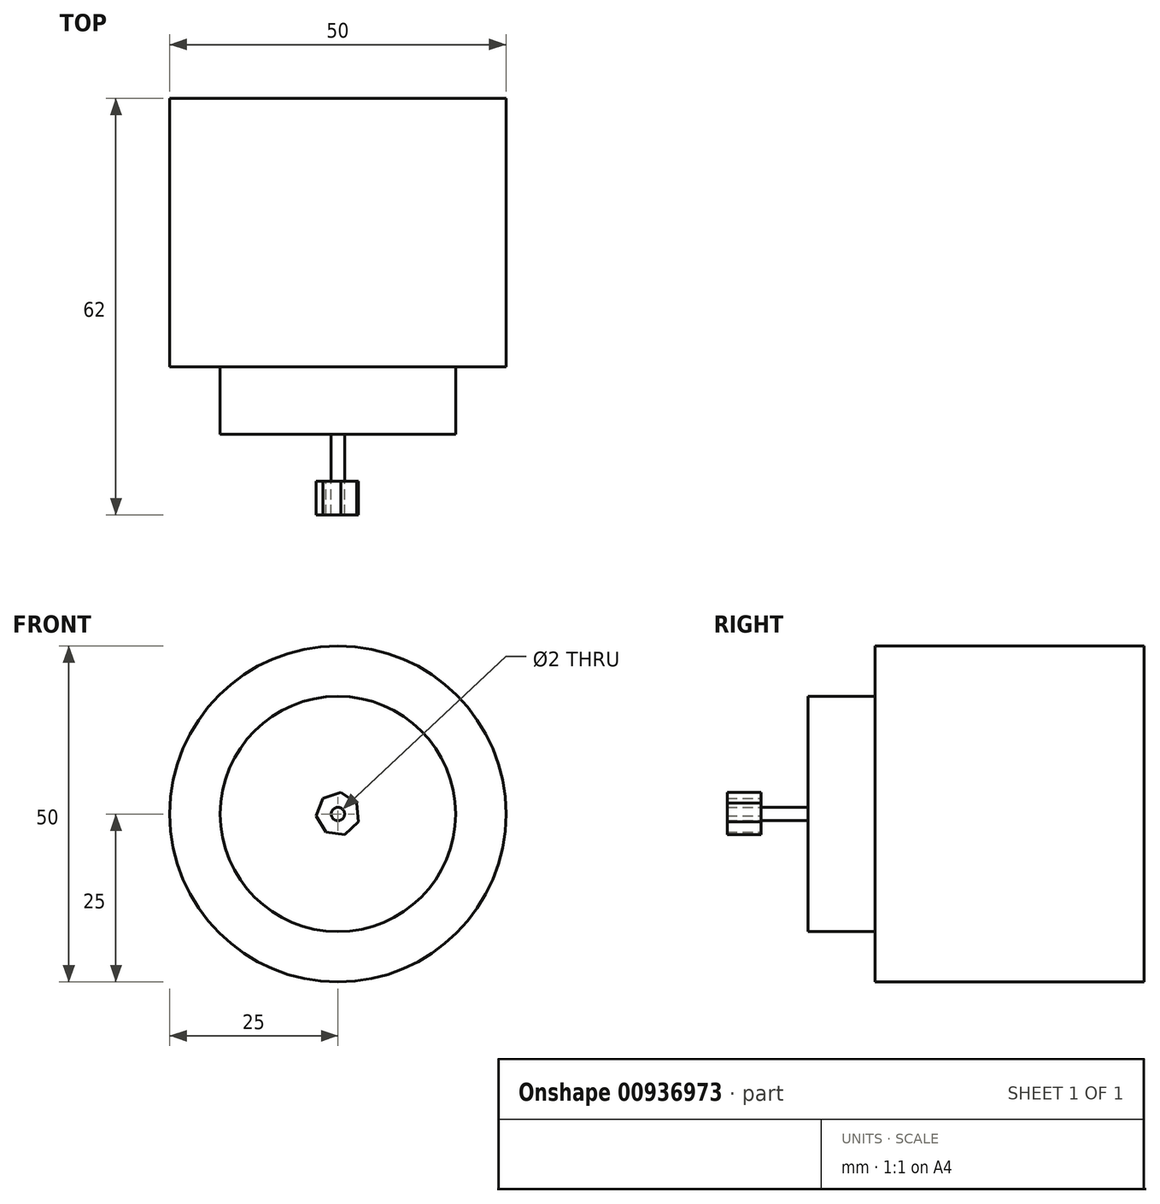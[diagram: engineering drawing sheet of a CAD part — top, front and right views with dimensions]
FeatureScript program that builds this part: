
annotation { "Feature Type Name" : "Feature", "Feature Type Description" : "" }
export const myFeature = defineFeature(function(context is Context, id is Id, definition is map)
    precondition{}
    {
        {
            var Q0;
            Q0=qCreatedBy(makeId("Front.planeOp"),FACE);
            var sketch = newSketch(context, id + "F0", { "sketchPlane" : qUnion([Q0])});
            skCircle(sketch, "E0", {"center": v(0, 0) * mm, "radius": 25 * mm});
            skSolve(sketch);
        }
        {
            var Q0;
            Q0 = qSketchRegion(id + "F0", true);
            extrude(context, id + "F1", {"entities" : qUnion([Q0]), "oppositeDirection" : true, "depth" : 40 * mm, "offsetDistance" : 25 * mm});
        }
        {
            var Q0;
            Q0=qCreatedBy(makeId("Front.planeOp"),FACE);
            var sketch = newSketch(context, id + "F2", { "sketchPlane" : qUnion([Q0])});
            skCircle(sketch, "E1", {"center": v(0, 0) * mm, "radius": 17.5 * mm});
            skSolve(sketch);
        }
        {
            var Q0;
            Q0=makeQuery(id+"F2.imprint","IMPRINT",FACE,{"disambiguationData":[TD([[makeQuery(id+"F2.imprint","IMPRINT",EDGE,{"derivedFrom":sQuery(id+"F2.wireOp",EDGE,"E1")}),1.0]])]});
            extrude(context, id + "F3", {"entities" : qUnion([Q0]), "depth" : 10 * mm, "offsetDistance" : 25 * mm});
        }
        {
            var Q0;
            Q0=makeQuery(id+"F3.opExtrude","CAP_FACE",FACE,{"disambiguationData":[OSD([sQuery(id+"F2.wireOp",EDGE,"E1")])],"isStart":false});
            var sketch = newSketch(context, id + "F4", { "sketchPlane" : qUnion([Q0])});
            skCircle(sketch, "E2", {"center": v(0, 0) * mm, "radius": 1 * mm});
            skSolve(sketch);
        }
        {
            var Q0;
            Q0 = qSketchRegion(id + "F4", true);
            extrude(context, id + "F5", {"entities" : qUnion([Q0]), "depth" : 7 * mm, "offsetDistance" : 25 * mm});
        }
        {
            var Q0;
            Q0=makeQuery(id+"F5.opExtrude","CAP_FACE",FACE,{"disambiguationData":[OSD([sQuery(id+"F4.wireOp",EDGE,"E2")])],"isStart":false});
            var sketch = newSketch(context, id + "F6", { "sketchPlane" : qUnion([Q0])});
            skCircle(sketch, "E3.cCircle", {"center": v(0, 0) * mm, "radius": 2.9 * mm, "construction": true});
            skLineSegment(sketch, "E3.0", {"start": v(0.45, 3.2) * mm, "end": v(2.78, 1.65) * mm});
            skLineSegment(sketch, "E3.1", {"start": v(2.78, 1.65) * mm, "end": v(3.02, -1.15) * mm});
            skLineSegment(sketch, "E3.2", {"start": v(3.02, -1.15) * mm, "end": v(0.99, -3.07) * mm});
            skLineSegment(sketch, "E3.3", {"start": v(0.99, -3.07) * mm, "end": v(-1.79, -2.69) * mm});
            skLineSegment(sketch, "E3.4", {"start": v(-1.79, -2.69) * mm, "end": v(-3.22, -0.28) * mm});
            skLineSegment(sketch, "E3.5", {"start": v(-3.22, -0.28) * mm, "end": v(-2.22, 2.34) * mm});
            skLineSegment(sketch, "E3.6", {"start": v(-2.22, 2.34) * mm, "end": v(0.45, 3.2) * mm});
            skPoint(sketch, "E3.0.midPoint", {"position": v(1.61, 2.42) * mm});
            skSolve(sketch);
        }
        {
            var Q0;
            Q0=makeQuery(id+"F6.imprint","IMPRINT",FACE,{"disambiguationData":[TD([[makeQuery(id+"F6.imprint","IMPRINT",EDGE,{"derivedFrom":sQuery(id+"F6.wireOp",EDGE,"E3.0")}),-1.0]])]});
            extrude(context, id + "F7", {"entities" : qUnion([Q0]), "depth" : 5 * mm, "offsetDistance" : 25 * mm});
        }
    });
